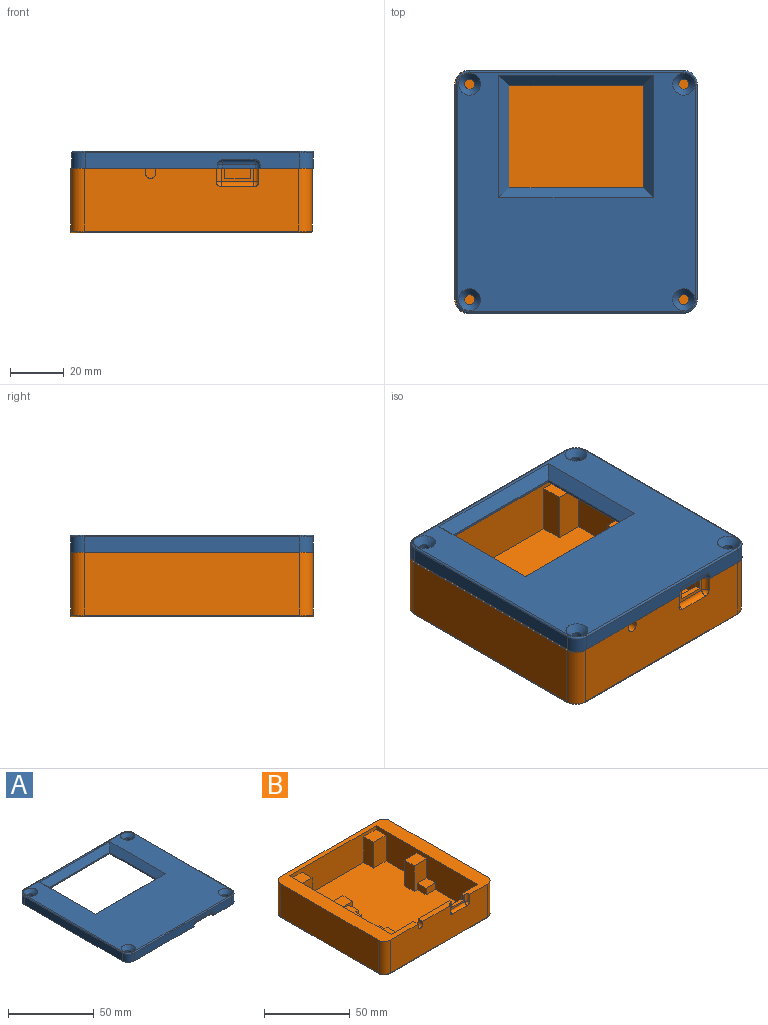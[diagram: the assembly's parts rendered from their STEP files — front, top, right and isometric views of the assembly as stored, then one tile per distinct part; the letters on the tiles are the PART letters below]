
ASSEMBLY  parts=2 mates=1
PART A: 49 faces, bbox 91x91.5x6.4 mm
  f0: plane 90.68x90.17mm, normal (0,0,-1), area 3568.1mm2, adj f3,f4,f5,f6,f7,f8,f9,f10
  f1: plane 72.39x42.93mm, normal (0,0,-1), area 1196.1mm2, adj f11,f12,f13,f14,f23,f24,f25,f26
  f2: plane 89.41x88.9mm, normal (0,0,1), area 5076.9mm2, adj f19,f20,f21,f22,f27,f28,f29,f30
  f3: plane 80.01x5.72mm, normal (0,1,0), area 457.3mm2, adj f0,f4,f10,f44
  f4: cylinder r=5.08mm len=5.72mm, axis (0,0,-1), area 45.6mm2, adj f0,f3,f5,f42
  f5: plane 80.52x5.72mm, normal (-1,0,0), area 460.2mm2, adj f0,f4,f6,f41
  f6: cylinder r=5.08mm len=5.72mm, axis (0,0,-1), area 45.6mm2, adj f0,f5,f7,f43
  f7: plane 80.01x5.72mm, normal (0,-1,0), area 408.4mm2, adj f0,f6,f8,f36,f37,f38,f39,f40
  f8: cylinder r=5.08mm len=5.72mm, axis (0,0,-1), area 45.6mm2, adj f0,f7,f9,f47
  f9: plane 80.52x5.72mm, normal (1,0,0), area 460.2mm2, adj f0,f8,f10,f48
  f10: cylinder r=5.08mm len=5.72mm, axis (0,0,-1), area 45.6mm2, adj f0,f3,f9,f46
  f11: plane 82.42x3.81mm, normal (1,0,0), area 221.4mm2, adj f0,f1,f12,f31,f33,f34
  f12: plane 72.39x1.65mm, normal (0,-1,0), area 119.5mm2, adj f0,f1,f11,f13
  f13: plane 42.93x1.65mm, normal (-1,0,0), area 70.9mm2, adj f0,f1,f12,f14
  f14: plane 36.83x1.65mm, normal (0,1,0), area 60.8mm2, adj f0,f1,f13,f32
  f15: cylinder r=1.91mm len=3.81mm, axis (0,0,1), area 45.6mm2, adj f0,f22
  f16: cylinder r=1.91mm len=3.81mm, axis (0,0,1), area 45.6mm2, adj f0,f21
  f17: cylinder r=1.91mm len=3.81mm, axis (0,0,1), area 45.6mm2, adj f0,f20
  f18: cylinder r=1.91mm len=3.81mm, axis (0,0,1), area 45.6mm2, adj f0,f19
  f19: cone r=1.91mm half-angle=41deg, axis (0,0,1), area 63.6mm2, adj f2,f18
  f20: cone r=1.91mm half-angle=41deg, axis (0,0,1), area 63.6mm2, adj f2,f17
  f21: cone r=1.91mm half-angle=41deg, axis (0,0,1), area 63.6mm2, adj f2,f16
  f22: cone r=1.91mm half-angle=41deg, axis (0,0,1), area 63.6mm2, adj f2,f15
  f23: plane 38.1x0.89mm, normal (1,0,0), area 33.9mm2, adj f1,f24,f26,f27
  f24: plane 50.17x0.89mm, normal (0,-1,0), area 44.6mm2, adj f1,f23,f25,f29
  f25: plane 38.1x0.89mm, normal (-1,0,0), area 33.9mm2, adj f1,f24,f26,f30
  f26: plane 50.17x0.89mm, normal (0,1,0), area 44.6mm2, adj f1,f23,f25,f28
  f27: plane 45.72x3.81mm, normal (0.71,0,0.71), area 225.8mm2, adj f2,f23,f28,f29
  f28: plane 57.79x3.81mm, normal (0,0.71,0.71), area 290.8mm2, adj f2,f26,f27,f30
  f29: plane 57.79x3.81mm, normal (0,-0.71,0.71), area 290.8mm2, adj f2,f24,f27,f30
  f30: plane 45.72x3.81mm, normal (-0.71,0,0.71), area 225.8mm2, adj f2,f25,f28,f29
  f31: plane 35.56x2.16mm, normal (0,-1,0), area 76.8mm2, adj f1,f11,f32,f34
  f32: plane 39.5x3.81mm, normal (-1,0,0), area 150.5mm2, adj f0,f14,f31,f33,f34
  f33: plane 35.56x3.81mm, normal (0,1,0), area 135.5mm2, adj f0,f11,f32,f34
  f34: plane 39.5x35.56mm, normal (0,0,-1), area 1404.5mm2, adj f11,f31,f32,f33
  f35: plane 12.07x1.27mm, normal (0,-1,0), area 15.3mm2, adj f0,f36,f38,f39
  f36: cylinder r=1.91mm len=1.91mm, axis (0,0,-1), area 3.8mm2, adj f0,f7,f35,f37
  f37: sphere r=1.91mm, area 5.7mm2, adj f7,f36,f39
  f38: cylinder r=1.91mm len=1.91mm, axis (0,0,1), area 3.8mm2, adj f0,f7,f35,f40
  f39: cylinder r=1.91mm len=12.07mm, axis (-1,0,0), area 36.1mm2, adj f7,f35,f37,f40
  f40: sphere r=1.91mm, area 5.7mm2, adj f7,f38,f39
  f41: cylinder r=0.64mm len=80.52mm, axis (0,1,0), area 80.3mm2, adj f2,f5,f42,f43
  f42: torus R=4.45mm, axis (0,0,1), area 7.6mm2, adj f2,f4,f41,f44
  f43: torus R=4.45mm, axis (0,0,1), area 7.6mm2, adj f2,f6,f41,f45
  f44: cylinder r=0.64mm len=80.01mm, axis (1,0,0), area 79.8mm2, adj f2,f3,f42,f46
  f45: cylinder r=0.64mm len=80.01mm, axis (-1,0,0), area 79.8mm2, adj f2,f7,f43,f47
  f46: torus R=4.45mm, axis (0,0,1), area 7.6mm2, adj f2,f10,f44,f48
  f47: torus R=4.45mm, axis (0,0,1), area 7.6mm2, adj f2,f8,f45,f48
  f48: cylinder r=0.64mm len=80.52mm, axis (0,-1,0), area 80.3mm2, adj f2,f9,f46,f47
PART B: 73 faces, bbox 91x91.5x24.1 mm
  f0: plane 25.84x3.81mm, normal (0,0,1), area 93.2mm2, adj f1,f3,f5,f64,f67,f72
  f1: plane 71.37x20.96mm, normal (0,1,0), area 1251mm2, adj f0,f2,f4,f5,f6,f7,f10,f24
  f2: plane 90.68x90.17mm, normal (0,0,1), area 2026.2mm2, adj f1,f3,f4,f16,f17,f18,f19,f20
  f3: plane 80.01x23.5mm, normal (0,-1,0), area 1757.5mm2, adj f0,f2,f19,f20,f60,f65,f66,f67
  f4: plane 3.81x1.91mm, normal (-1,0,0), area 7.3mm2, adj f1,f2,f6,f64
  f5: plane 3.81x1.91mm, normal (1,0,0), area 7.3mm2, adj f0,f1,f6,f64
  f6: plane 9.53x1.91mm, normal (0,0,1), area 18.1mm2, adj f1,f4,f5,f64
  f7: plane 41.91x17.4mm, normal (1,0,0), area 556.3mm2, adj f1,f8,f9,f36,f38,f39,f40,f42
  f8: plane 12.07x7.11mm, normal (0,0,1), area 76.8mm2, adj f7,f26,f38,f49,f50,f54
  f9: plane 7.62x6.99mm, normal (0,0,1), area 53.2mm2, adj f7,f12,f38,f41,f42
  f10: plane 7.62x6.99mm, normal (0,0,1), area 53.2mm2, adj f1,f24,f45,f46
  f11: plane 7.62x6.99mm, normal (0,0,1), area 53.2mm2, adj f24,f37,f47,f48
  f12: plane 4.7x4.45mm, normal (0,1,0), area 20.9mm2, adj f9,f32,f36,f41
  f13: plane 10.29x8.19mm, normal (0,0,1), area 84.3mm2, adj f26,f31,f32,f38
  f14: plane 10.29x8.19mm, normal (0,0,1), area 84.3mm2, adj f24,f33,f34,f37
  f15: plane 10.29x8.19mm, normal (0,0,1), area 84.3mm2, adj f24,f25,f28,f35
  f16: plane 80.01x23.5mm, normal (0,1,0), area 1879.8mm2, adj f2,f17,f22,f59
  f17: cylinder r=5.08mm len=23.5mm, axis (0,0,1), area 187.5mm2, adj f2,f16,f18,f57
  f18: plane 80.52x23.5mm, normal (-1,0,0), area 1891.8mm2, adj f2,f17,f19,f56
  f19: cylinder r=5.08mm len=23.5mm, axis (0,0,1), area 187.5mm2, adj f2,f3,f18,f58
  f20: cylinder r=5.08mm len=23.5mm, axis (0,0,1), area 187.5mm2, adj f2,f3,f21,f62
  f21: plane 80.52x23.5mm, normal (1,0,0), area 1891.8mm2, adj f2,f20,f22,f63
  f22: cylinder r=5.08mm len=23.5mm, axis (0,0,1), area 187.5mm2, adj f2,f16,f21,f61
  f23: plane 89.41x88.9mm, normal (0,0,-1), area 7931.4mm2, adj f56,f57,f58,f59,f60,f61,f62,f63
  f24: plane 83.69x20.96mm, normal (-1,0,0), area 1386.4mm2, adj f1,f2,f10,f11,f14,f15,f25,f34
  f25: plane 71.37x20.96mm, normal (0,-1,0), area 1116.8mm2, adj f2,f15,f24,f26,f27,f28,f29,f36
  f26: plane 83.69x20.96mm, normal (1,0,0), area 790.6mm2, adj f1,f2,f8,f13,f25,f27,f30,f31
  f27: plane 10.29x8.19mm, normal (0,0,1), area 84.3mm2, adj f25,f26,f29,f30
  f28: plane 18.42x8.19mm, normal (-1,0,0), area 150.8mm2, adj f15,f25,f35,f36
  f29: plane 18.42x8.19mm, normal (1,0,0), area 150.8mm2, adj f25,f27,f30,f36
  f30: plane 18.42x10.29mm, normal (0,-1,0), area 189.4mm2, adj f26,f27,f29,f36
  f31: plane 18.42x10.29mm, normal (0,1,0), area 189.4mm2, adj f13,f26,f32,f36
  f32: plane 18.42x8.19mm, normal (1,0,0), area 150.8mm2, adj f12,f13,f31,f36,f38
  f33: plane 18.42x8.19mm, normal (-1,0,0), area 150.8mm2, adj f14,f34,f36,f37
  f34: plane 18.42x10.29mm, normal (0,1,0), area 189.4mm2, adj f14,f24,f33,f36
  f35: plane 18.42x10.29mm, normal (0,-1,0), area 189.4mm2, adj f15,f24,f28,f36
  f36: plane 83.69x71.37mm, normal (0,0,1), area 5125.5mm2, adj f1,f7,f12,f24,f25,f26,f28,f29
  f37: plane 18.42x10.29mm, normal (0,-1,0), area 153.6mm2, adj f11,f14,f24,f33,f36,f48
  f38: plane 13.72x10.29mm, normal (0,-1,0), area 50.8mm2, adj f7,f8,f9,f13,f26,f32
  f39: plane 7.62x6.99mm, normal (0,0,1), area 53.2mm2, adj f1,f7,f43,f44
  f40: plane 14.61x7.11mm, normal (0,0,1), area 94.8mm2, adj f1,f7,f26,f51,f52,f53
  f41: plane 6.99x4.7mm, normal (1,0,0), area 32.8mm2, adj f9,f12,f36,f42
  f42: plane 7.62x4.7mm, normal (0,-1,0), area 35.8mm2, adj f7,f9,f36,f41
  f43: plane 7.62x4.7mm, normal (0,1,0), area 35.8mm2, adj f7,f36,f39,f44
  f44: plane 6.99x4.7mm, normal (1,0,0), area 32.8mm2, adj f1,f36,f39,f43
  f45: plane 6.99x4.7mm, normal (-1,0,0), area 32.8mm2, adj f1,f10,f36,f46
  f46: plane 7.62x4.7mm, normal (0,1,0), area 35.8mm2, adj f10,f24,f36,f45
  f47: plane 7.62x4.7mm, normal (0,-1,0), area 35.8mm2, adj f11,f24,f36,f48
  f48: plane 6.99x4.7mm, normal (-1,0,0), area 32.8mm2, adj f11,f36,f37,f47
  f49: plane 4.45x4.45mm, normal (1,0,0), area 19.8mm2, adj f8,f50,f54,f55
  f50: plane 5.08x4.45mm, normal (0,-1,0), area 22.6mm2, adj f8,f26,f49,f55
  f51: plane 5.08x4.45mm, normal (0,1,0), area 22.6mm2, adj f26,f40,f52,f55
  f52: plane 4.45x4.45mm, normal (1,0,0), area 19.8mm2, adj f40,f51,f53,f55
  f53: plane 4.45x2.03mm, normal (0,1,0), area 9mm2, adj f7,f40,f52,f55
  f54: plane 4.45x2.03mm, normal (0,-1,0), area 9mm2, adj f7,f8,f49,f55
  f55: plane 24.13x7.11mm, normal (0,0,1), area 126.5mm2, adj f7,f26,f49,f50,f51,f52,f53,f54
  f56: cylinder r=0.64mm len=80.52mm, axis (0,1,0), area 80.3mm2, adj f18,f23,f57,f58
  f57: torus R=4.45mm, axis (0,0,1), area 7.6mm2, adj f17,f23,f56,f59
  f58: torus R=4.45mm, axis (0,0,1), area 7.6mm2, adj f19,f23,f56,f60
  f59: cylinder r=0.64mm len=80.01mm, axis (1,0,0), area 79.8mm2, adj f16,f23,f57,f61
  f60: cylinder r=0.64mm len=80.01mm, axis (-1,0,0), area 79.8mm2, adj f3,f23,f58,f62
  f61: torus R=4.45mm, axis (0,0,1), area 7.6mm2, adj f22,f23,f59,f63
  f62: torus R=4.45mm, axis (0,0,1), area 7.6mm2, adj f20,f23,f60,f63
  f63: cylinder r=0.64mm len=80.52mm, axis (0,-1,0), area 80.3mm2, adj f21,f23,f61,f62
  f64: plane 12.07x5.08mm, normal (0,-1,0), area 25mm2, adj f0,f2,f4,f5,f6,f65,f67,f68
  f65: cylinder r=1.91mm len=5.08mm, axis (0,0,1), area 15.2mm2, adj f2,f3,f64,f66
  f66: sphere r=1.91mm, area 5.7mm2, adj f3,f65,f68
  f67: cylinder r=1.91mm len=5.08mm, axis (0,0,-1), area 15.2mm2, adj f0,f3,f64,f69
  f68: cylinder r=1.91mm len=12.07mm, axis (1,0,0), area 36.1mm2, adj f3,f64,f66,f69
  f69: sphere r=1.91mm, area 5.7mm2, adj f3,f67,f68
  f70: plane 3.81x1.91mm, normal (1,0,0), area 7.3mm2, adj f1,f2,f3,f71
  f71: cylinder r=1.91mm len=3.81mm, axis (0,-1,0), area 22.8mm2, adj f1,f3,f70,f72
  f72: plane 3.81x1.91mm, normal (-1,0,0), area 7.3mm2, adj f0,f1,f3,f71
PLACE A t=(-143.28,37.01,17.26)mm
PLACE B t=(-143.79,37.01,17.26)mm
MATE fastened A.f0 <-> B.f2  axis (0,0,-1) through (-134.39,33.84,17.26)mm
